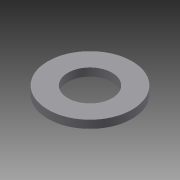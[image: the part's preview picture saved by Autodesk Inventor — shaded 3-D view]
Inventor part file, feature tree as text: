
AUTODESK INVENTOR PART (.ipt)
format: ipt  version: 2013 (Build 170138000, 138)  size: 73,216 bytes
history: native  units: mm
features: extrude x1, sketch x1
ambient origin geometry x8: Origin, YZ Plane, XZ Plane, XY Plane, X Axis, Y Axis, Z Axis, Center Point
bodies: Solid1 (feature_tree)
feature tree (2):
  extrude  "Extrusion1"  Depth=16.0mm
  sketch  "Sketch1"  dims[d0=8.4mm d2=16.0mm d3=1.5mm d4=0.0mm]
